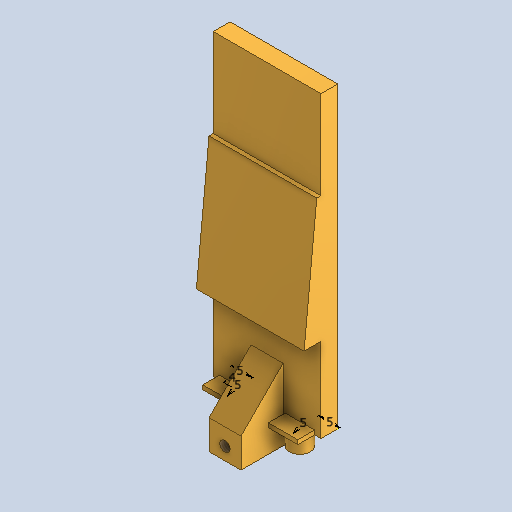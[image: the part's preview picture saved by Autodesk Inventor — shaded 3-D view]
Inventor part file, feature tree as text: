
AUTODESK INVENTOR PART (.ipt)
format: ipt  version: 2025 (Build 290162010, 162A)  size: 247,808 bytes
history: native  units: mm
features: sketch x7, extrude x6, chamfer x2, hole x1, projected_geometry x1
ambient origin geometry x8: Origin, YZ Plane, XZ Plane, XY Plane, X Axis, Y Axis, Z Axis, Center Point
bodies: Volumenkörper1 (feature_tree)
feature tree (17):
  extrude  "Extrusion1"  Depth=25.6mm
  extrude  "Extrusion2"  Depth=5.0mm
  extrude  "Extrusion3"  Depth=5.0mm
  chamfer  "Fasen1"  Distance=5.0mm
  extrude  "Extrusion4"  Depth=77.0mm
  extrude  "Extrusion5"  Depth=6.0mm
  extrude  "Extrusion6"  Depth=6.0mm
  hole  "Bohrung1"  [1 undecoded]
  chamfer  "Fasen2"  Distance=16.0mm
  sketch  "Skizze1"  dims[d7=4.0mm d8=0.0mm d9=25.6mm]
  sketch  "Skizze2"  dims[d18=2.459mm d19=6.0mm d20=4.0mm d21=2.0mm d22=90.0deg d23=8.0mm d24=20.594885mm d29=5.0mm]
  sketch  "Skizze3"  dims[d31=4.0mm d32=0.0mm d34=40.0mm d35=5.0mm d36=0.0mm]
  sketch  "Skizze4"  dims[d39=40.0mm d40=4.0mm d41=45.0deg d48=77.0mm]
  sketch  "Skizze5"  dims[d49=9.0mm d50=6.0mm]
  projected_geometry  "Projizierte Kontur1"
  sketch  "Skizze6"  dims[d51=9.0mm d52=6.0mm]
  sketch  "Skizze7"  dims[d53=3.0mm d54=5.0mm d57=16.0mm d58=10.0mm d59=0.0mm d60=7.0mm d61=1.0mm d62=7.0mm d63=1.0mm d64=4.0mm d65=0.0mm d66=4.0mm d69=5.0mm d70=5.0mm d71=7.0mm d72=10.0mm d73=0.0mm d74=10.0mm d75=2.0mm d76=45.0deg]
note: 1 required parameter value undecoded (feature->parameter linkage not recoverable at this tier; creation-order binding heuristic only, values carry confidence <= 0.55)
